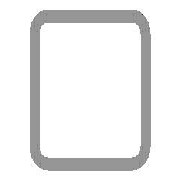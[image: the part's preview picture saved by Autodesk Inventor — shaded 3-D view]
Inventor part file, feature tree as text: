
AUTODESK INVENTOR PART (.ipt)
format: ipt  version: 2025 (Build 290162010, 162A)  size: 134,144 bytes
history: native  units: mm (DEFAULTED — no unit token found)
features: other x4, sketch x1, plane x1
ambient origin geometry x8: Origin, YZ Plane, XZ Plane, XY Plane, X Axis, Y Axis, Z Axis, Center Point
bodies: Solid1 (feature_tree), Body (feature_tree)
feature tree (6):
  parser-record x1  (decoder bookkeeping rows leaked as tree rows — omitted from the tree; the rows remain in map.json)
  other  "Driven Length"
  other  "Start Plane"
  other  "End Plane"
  sketch  "Sketch3"  dims[d3=4405.0mm d4=0.0mm d7=6.0mm d9=80.0mm d11=80.0mm d12=3.0mm d13=-0.0mm d14=4405.0mm d15=40.0mm d16=40.0mm d17=90.0deg d18=4405.0mm]
  plane  "Work Plane3"
